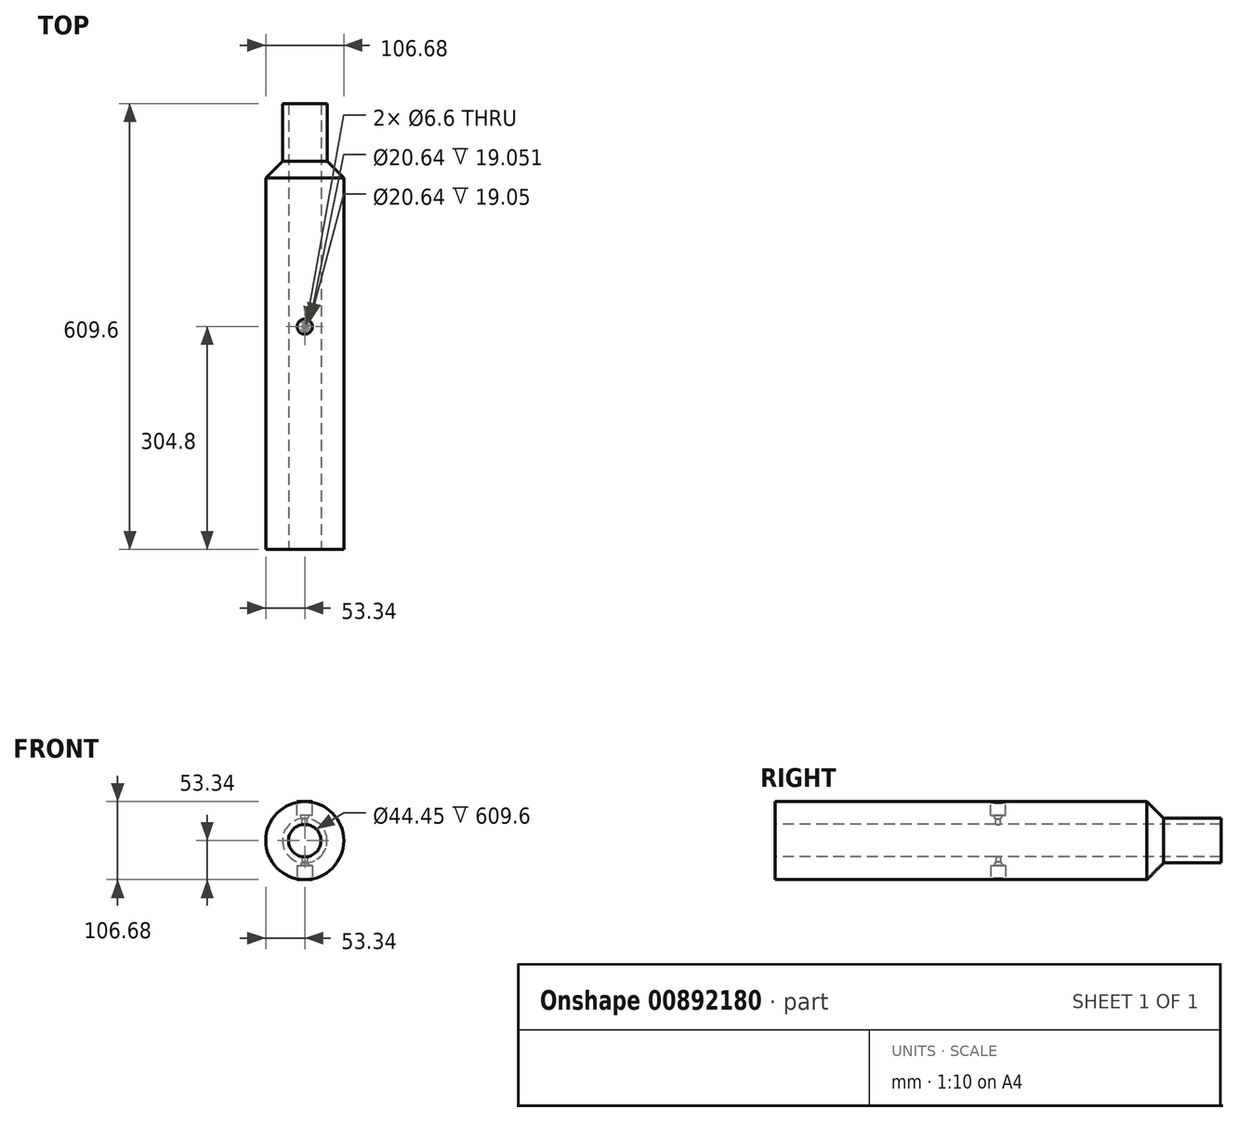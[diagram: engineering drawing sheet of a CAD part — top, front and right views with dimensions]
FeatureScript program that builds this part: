
annotation { "Feature Type Name" : "Feature", "Feature Type Description" : "" }
export const myFeature = defineFeature(function(context is Context, id is Id, definition is map)
    precondition{}
    {
        {
            var Q0;
            Q0=qCreatedBy(makeId("Front.planeOp"),FACE);
            var sketch = newSketch(context, id + "F0", { "sketchPlane" : qUnion([Q0])});
            skCircle(sketch, "E0", {"center": v(0, 0) * mm, "radius": 22.23 * mm});
            skCircle(sketch, "E1", {"center": v(0, 0) * mm, "radius": 53.34 * mm});
            skSolve(sketch);
        }
        {
            var Q0;
            Q0=makeQuery(id+"F0.imprint","IMPRINT",FACE,{"disambiguationData":[TD([[makeQuery(id+"F0.imprint","IMPRINT",EDGE,{"derivedFrom":sQuery(id+"F0.wireOp",EDGE,"E0")}),-1.0]])]});
            extrude(context, id + "F1", {"entities" : qUnion([Q0]), "endBound" : BoundingType.SYMMETRIC, "oppositeDirection" : true, "depth" : 609.6 * mm, "offsetDistance" : 25.4 * mm});
        }
        {
            var Q0;
            Q0=makeQuery(id+"F1.opExtrude","CAP_FACE",FACE,{"disambiguationData":[OSD([sQuery(id+"F0.wireOp",EDGE,"E0"),sQuery(id+"F0.wireOp",EDGE,"E1")])],"isStart":false});
            cPlane(context, id + "F2", {"entities" : qUnion([Q0]), "cplaneType" : CPlaneType.OFFSET, "offset" : 0 * mm, "oppositeDirection" : true, "width" : 152.4 * mm, "height" : 152.4 * mm});
        }
        {
            var Q0;
            Q0=qCreatedBy(makeId("Front.planeOp"),FACE);
            cPlane(context, id + "F3", {"entities" : qUnion([Q0]), "cplaneType" : CPlaneType.OFFSET, "offset" : 203.2 * mm, "oppositeDirection" : true, "width" : 152.4 * mm, "height" : 152.4 * mm});
        }
        {
            var Q0;
            Q0=qCreatedBy(id+"F2.planeOp",FACE);
            var sketch = newSketch(context, id + "F4", { "sketchPlane" : qUnion([Q0])});
            skCircle(sketch, "E2", {"center": v(0, 0) * mm, "radius": 22.23 * mm});
            skCircle(sketch, "E3", {"center": v(0, 0) * mm, "radius": 30.48 * mm});
            skCircle(sketch, "E4", {"center": v(0, 0) * mm, "radius": 53.34 * mm});
            skSolve(sketch);
        }
        {
            var Q0;
            Q0=makeQuery(id+"F4.imprint","IMPRINT",FACE,{"disambiguationData":[TD([[makeQuery(id+"F4.imprint","IMPRINT",EDGE,{"derivedFrom":sQuery(id+"F4.wireOp",EDGE,"E3")}),-1.0]])]});
            var Q1;
            Q1=qCreatedBy(id+"F3.planeOp",FACE);
            extrude(context, id + "F5", {"entities" : qUnion([Q0]), "operationType" : NewBodyOperationType.REMOVE, "oppositeDirection" : true, "depth" : 101.6 * mm, "endBoundEntityFace" : qUnion([Q1]), "offsetDistance" : 25.4 * mm});
        }
        {
            var Q0;
            Q0=qCreatedBy(makeId("Right.planeOp"),FACE);
            var sketch = newSketch(context, id + "F6", { "sketchPlane" : qUnion([Q0])});
            skLineSegment(sketch, "E5", {"start": v(0, 0) * mm, "end": v(203.2, 0) * mm, "construction": true});
            skLineSegment(sketch, "E6", {"start": v(203.2, 0) * mm, "end": v(203.2, 53.34) * mm});
            skLineSegment(sketch, "E7", {"start": v(203.2, 0) * mm, "end": v(203.2, 30.48) * mm});
            skLineSegment(sketch, "E8", {"start": v(203.2, 30.48) * mm, "end": v(226.06, 30.48) * mm});
            skLineSegment(sketch, "E9", {"start": v(226.06, 30.48) * mm, "end": v(203.2, 53.34) * mm});
            skSolve(sketch);
        }
        {
            var Q0;
            Q0=makeQuery(id+"F6.imprint","IMPRINT",FACE,{"disambiguationData":[TD([[makeQuery(id+"F6.imprint","IMPRINT",EDGE,{"derivedFrom":sQuery(id+"F6.wireOp",EDGE,"E6")}),-1.0]])]});
            var Q1;
            Q1=sQuery(id+"F6.wireOp",EDGE,"E5");
            revolve(context, id + "F7", {"operationType" : NewBodyOperationType.ADD, "surfaceOperationType" : NewSurfaceOperationType.NEW, "entities" : qUnion([Q0]), "axis" : qUnion([Q1]), "revolveType" : RevolveType.FULL});
        }
        {
            var Q0;
            Q0=qCreatedBy(makeId("Top.planeOp"),FACE);
            cPlane(context, id + "F8", {"entities" : qUnion([Q0]), "cplaneType" : CPlaneType.OFFSET, "offset" : 53.34 * mm, "width" : 152.4 * mm, "height" : 152.4 * mm});
        }
        {
            var Q0;
            Q0=qCreatedBy(makeId("Top.planeOp"),FACE);
            cPlane(context, id + "F9", {"entities" : qUnion([Q0]), "cplaneType" : CPlaneType.OFFSET, "offset" : 53.34 * mm, "oppositeDirection" : true, "width" : 152.4 * mm, "height" : 152.4 * mm});
        }
        {
            var Q0;
            Q0=qCreatedBy(id+"F8.planeOp",FACE);
            var sketch = newSketch(context, id + "F10", { "sketchPlane" : qUnion([Q0])});
            skCircle(sketch, "E10", {"center": v(0, 0) * mm, "radius": 10.32 * mm});
            skCircle(sketch, "E11", {"center": v(0, 0) * mm, "radius": 3.3 * mm});
            skSolve(sketch);
        }
        {
            var Q0;
            Q0=makeQuery(id+"F10.imprint","IMPRINT",FACE,{"disambiguationData":[TD([[makeQuery(id+"F10.imprint","IMPRINT",EDGE,{"derivedFrom":sQuery(id+"F10.wireOp",EDGE,"E10")}),1.0]])]});
            var Q1;
            Q1=makeQuery(id+"F10.imprint","IMPRINT",FACE,{"disambiguationData":[TD([[makeQuery(id+"F10.imprint","IMPRINT",EDGE,{"derivedFrom":sQuery(id+"F10.wireOp",EDGE,"E11")}),1.0]])]});
            extrude(context, id + "F11", {"entities" : qUnion([Q0, Q1]), "operationType" : NewBodyOperationType.REMOVE, "oppositeDirection" : true, "depth" : 19.05 * mm, "offsetDistance" : 25.4 * mm});
        }
        {
            var Q0;
            Q0=makeQuery(id+"F10.imprint","IMPRINT",FACE,{"disambiguationData":[TD([[makeQuery(id+"F10.imprint","IMPRINT",EDGE,{"derivedFrom":sQuery(id+"F10.wireOp",EDGE,"E11")}),1.0]])]});
            var Q1;
            Q1=makeQuery(id+"F1.opExtrude","SWEPT_FACE",FACE,{"disambiguationData":[OSD([sQuery(id+"F0.wireOp",EDGE,"E0")])]});
            extrude(context, id + "F12", {"entities" : qUnion([Q0]), "operationType" : NewBodyOperationType.REMOVE, "endBound" : BoundingType.UP_TO_SURFACE, "oppositeDirection" : true, "depth" : 27.94 * mm, "endBoundEntityFace" : qUnion([Q1]), "offsetDistance" : 25.4 * mm});
        }
        {
            var Q0;
            Q0=qCreatedBy(id+"F9.planeOp",FACE);
            var sketch = newSketch(context, id + "F13", { "sketchPlane" : qUnion([Q0])});
            skCircle(sketch, "E12", {"center": v(0, 0) * mm, "radius": 10.32 * mm});
            skCircle(sketch, "E13", {"center": v(0, 0) * mm, "radius": 3.3 * mm});
            skSolve(sketch);
        }
        {
            var Q0;
            Q0=makeQuery(id+"F13.imprint","IMPRINT",FACE,{"disambiguationData":[TD([[makeQuery(id+"F13.imprint","IMPRINT",EDGE,{"derivedFrom":sQuery(id+"F13.wireOp",EDGE,"E12")}),1.0]])]});
            var Q1;
            Q1=makeQuery(id+"F13.imprint","IMPRINT",FACE,{"disambiguationData":[TD([[makeQuery(id+"F13.imprint","IMPRINT",EDGE,{"derivedFrom":sQuery(id+"F13.wireOp",EDGE,"E13")}),1.0]])]});
            extrude(context, id + "F14", {"entities" : qUnion([Q0, Q1]), "operationType" : NewBodyOperationType.REMOVE, "depth" : 19.05 * mm, "offsetDistance" : 25.4 * mm});
        }
        {
            var Q0;
            Q0=makeQuery(id+"F13.imprint","IMPRINT",FACE,{"disambiguationData":[TD([[makeQuery(id+"F13.imprint","IMPRINT",EDGE,{"derivedFrom":sQuery(id+"F13.wireOp",EDGE,"E13")}),1.0]])]});
            var Q1;
            Q1=makeQuery(id+"F1.opExtrude","SWEPT_FACE",FACE,{"disambiguationData":[OSD([sQuery(id+"F0.wireOp",EDGE,"E0")])]});
            extrude(context, id + "F15", {"entities" : qUnion([Q0]), "operationType" : NewBodyOperationType.REMOVE, "endBound" : BoundingType.UP_TO_SURFACE, "depth" : 27.94 * mm, "endBoundEntityFace" : qUnion([Q1]), "offsetDistance" : 25.4 * mm});
        }
        {
            var Q0;
            Q0=qCreatedBy(makeId("Right.planeOp"),FACE);
            var sketch = newSketch(context, id + "F16", { "sketchPlane" : qUnion([Q0])});
            skLineSegment(sketch, "E14", {"start": v(0, 0) * mm, "end": v(0, 34.3) * mm, "construction": true});
            skLineSegment(sketch, "E15", {"start": v(3.3, 34.3) * mm, "end": v(6.35, 34.3) * mm});
            skLineSegment(sketch, "E16", {"start": v(0, 0) * mm, "end": v(3.3, 0) * mm, "construction": true});
            skLineSegment(sketch, "E17", {"start": v(3.3, 29.21) * mm, "end": v(6.35, 34.3) * mm});
            skLineSegment(sketch, "E18", {"start": v(3.3, 29.21) * mm, "end": v(3.3, 34.3) * mm});
            skLineSegment(sketch, "E19.MirrorCS", {"start": v(3.3, -29.21) * mm, "end": v(3.3, -34.3) * mm});
            skLineSegment(sketch, "E20.MirrorCS", {"start": v(3.3, -34.3) * mm, "end": v(6.35, -34.3) * mm});
            skLineSegment(sketch, "E21.MirrorCS", {"start": v(3.3, -29.21) * mm, "end": v(6.35, -34.3) * mm});
            skSolve(sketch);
        }
        {
            var Q0;
            Q0=qSketchRegion(id+"F16",true);
            var Q1;
            Q1=sQuery(id+"F16.wireOp",EDGE,"E14");
            revolve(context, id + "F17", {"operationType" : NewBodyOperationType.REMOVE, "surfaceOperationType" : NewSurfaceOperationType.NEW, "entities" : qUnion([Q0]), "axis" : qUnion([Q1]), "revolveType" : RevolveType.FULL, "oppositeDirection" : true});
        }
        {
            var Q0;
            Q0=qCreatedBy(makeId("Right.planeOp"),FACE);
            var sketch = newSketch(context, id + "F18", { "sketchPlane" : qUnion([Q0])});
            skLineSegment(sketch, "E22", {"start": v(0, 34.3) * mm, "end": v(-6.35, 34.3) * mm});
            skLineSegment(sketch, "E23", {"start": v(0, 0) * mm, "end": v(-3.3, 0) * mm});
            skLineSegment(sketch, "E24", {"start": v(-3.3, 29.21) * mm, "end": v(-6.35, 34.3) * mm});
            skLineSegment(sketch, "E25", {"start": v(-3.3, 29.21) * mm, "end": v(0, 29.21) * mm});
            skLineSegment(sketch, "E26", {"start": v(0, 29.21) * mm, "end": v(0, 34.3) * mm});
            skLineSegment(sketch, "E27", {"start": v(0, 29.21) * mm, "end": v(0, 0) * mm, "construction": true});
            skLineSegment(sketch, "E28.MirrorCS", {"start": v(-3.3, -29.21) * mm, "end": v(0, -29.21) * mm});
            skLineSegment(sketch, "E29.MirrorCS", {"start": v(0, -29.21) * mm, "end": v(0, -34.3) * mm});
            skLineSegment(sketch, "E30.MirrorCS", {"start": v(-3.3, -29.21) * mm, "end": v(-6.35, -34.3) * mm});
            skLineSegment(sketch, "E31.MirrorCS", {"start": v(0, -34.3) * mm, "end": v(-6.35, -34.3) * mm});
            skSolve(sketch);
        }
        {
            var Q0;
            Q0 = qSketchRegion(id + "F18", true);
            var Q1;
            Q1=sQuery(id+"F18.wireOp",EDGE,"E27");
            revolve(context, id + "F19", {"surfaceOperationType" : NewSurfaceOperationType.NEW, "entities" : qUnion([Q0]), "axis" : qUnion([Q1]), "revolveType" : RevolveType.FULL});
        }
        {
            var Q0;
            Q0=qCreatedBy(id+"F8.planeOp",FACE);
            var sketch = newSketch(context, id + "F20", { "sketchPlane" : qUnion([Q0])});
            skCircle(sketch, "E32", {"center": v(0, 0) * mm, "radius": 10.32 * mm});
            skSolve(sketch);
        }
        {
            var Q0;
            Q0 = qSketchRegion(id + "F20", true);
            var Q1;
            Q1=makeQuery(id+"F11.boolean.opBoolean","COPY",FACE,{"derivedFrom":makeQuery(id+"F11.opExtrude","CAP_FACE",FACE,{"disambiguationData":[OSD([sQuery(id+"F10.wireOp",EDGE,"E10")])],"isStart":false})});
            extrude(context, id + "F21", {"entities" : qUnion([Q0]), "endBound" : BoundingType.UP_TO_SURFACE, "oppositeDirection" : true, "depth" : 25.4 * mm, "endBoundEntityFace" : qUnion([Q1]), "offsetDistance" : 25.4 * mm});
        }
        {
            var Q0;
            Q0=qCreatedBy(id+"F9.planeOp",FACE);
            var sketch = newSketch(context, id + "F22", { "sketchPlane" : qUnion([Q0])});
            skCircle(sketch, "E33", {"center": v(0, 0) * mm, "radius": 10.32 * mm});
            skSolve(sketch);
        }
        {
            var Q0;
            Q0 = qSketchRegion(id + "F22", true);
            var Q1;
            Q1=makeQuery(id+"F14.boolean.opBoolean","COPY",FACE,{"derivedFrom":makeQuery(id+"F14.opExtrude","CAP_FACE",FACE,{"disambiguationData":[OSD([sQuery(id+"F13.wireOp",EDGE,"E12")])],"isStart":false})});
            extrude(context, id + "F23", {"entities" : qUnion([Q0]), "endBound" : BoundingType.UP_TO_SURFACE, "depth" : 25.4 * mm, "endBoundEntityFace" : qUnion([Q1]), "offsetDistance" : 25.4 * mm});
        }
    });
